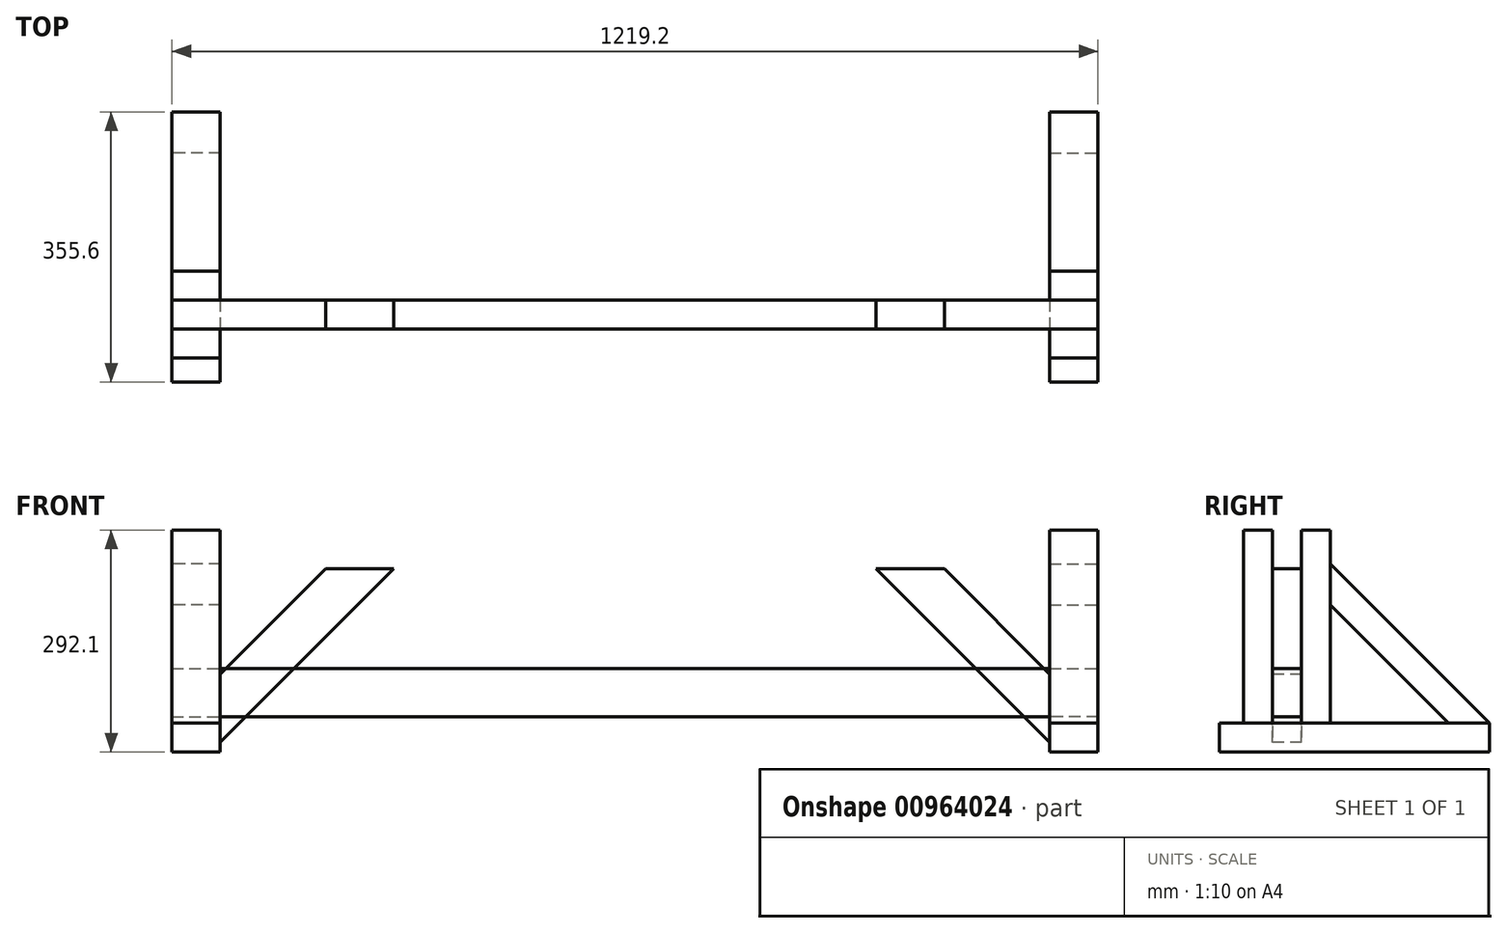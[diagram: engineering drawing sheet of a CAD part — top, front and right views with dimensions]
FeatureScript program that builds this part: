
annotation { "Feature Type Name" : "Feature", "Feature Type Description" : "" }
export const myFeature = defineFeature(function(context is Context, id is Id, definition is map)
    precondition{}
    {
        {
            assignVariable(context, id + "F0", {"name" : "shortLength", "anyValue" : 8});
        }
        {
            var Q0;
            Q0=qCreatedBy(makeId("Top.planeOp"),FACE);
            var sketch = newSketch(context, id + "F1", { "sketchPlane" : qUnion([Q0])});
            skLineSegment(sketch, "E0.bottom", {"start": v(-609.6, 254) * mm, "end": v(-546.1, 254) * mm});
            skLineSegment(sketch, "E0.top", {"start": v(-609.6, -101.6) * mm, "end": v(-546.1, -101.6) * mm});
            skLineSegment(sketch, "E0.left", {"start": v(-609.6, 254) * mm, "end": v(-609.6, -101.6) * mm});
            skLineSegment(sketch, "E0.right", {"start": v(-546.1, 254) * mm, "end": v(-546.1, -101.6) * mm});
            skLineSegment(sketch, "E1", {"start": v(-577.85, 254) * mm, "end": v(-577.85, -101.6) * mm, "construction": true});
            skSolve(sketch);
        }
        {
            var Q0;
            Q0=makeQuery(id+"F1.imprint","IMPRINT",FACE,{"disambiguationData":[TD([[makeQuery(id+"F1.imprint","IMPRINT",EDGE,{"derivedFrom":sQuery(id+"F1.wireOp",EDGE,"E0.bottom")}),-1.0]])]});
            extrude(context, id + "F2", {"entities" : qUnion([Q0]), "depth" : 38.1 * mm, "offsetDistance" : 25.4 * mm});
        }
        {
            var Q0;
            Q0=makeQuery(id+"F2.opExtrude","CAP_FACE",FACE,{"disambiguationData":[OSD([sQuery(id+"F1.wireOp",EDGE,"E0.bottom"),sQuery(id+"F1.wireOp",EDGE,"E0.top"),sQuery(id+"F1.wireOp",EDGE,"E0.left"),sQuery(id+"F1.wireOp",EDGE,"E0.right")])],"isStart":false});
            var sketch = newSketch(context, id + "F3", { "sketchPlane" : qUnion([Q0])});
            skLineSegment(sketch, "E2.bottom", {"start": v(-609.6, 6.35) * mm, "end": v(-546.1, 6.35) * mm});
            skLineSegment(sketch, "E2.top", {"start": v(-609.6, -31.75) * mm, "end": v(-546.1, -31.75) * mm});
            skLineSegment(sketch, "E2.left", {"start": v(-609.6, 6.35) * mm, "end": v(-609.6, -31.75) * mm});
            skLineSegment(sketch, "E2.right", {"start": v(-546.1, 6.35) * mm, "end": v(-546.1, -31.75) * mm});
            skSolve(sketch);
        }
        {
            var Q0;
            Q0=makeQuery(id+"F3.imprint","IMPRINT",FACE,{"disambiguationData":[TD([[makeQuery(id+"F3.imprint","IMPRINT",EDGE,{"derivedFrom":sQuery(id+"F3.wireOp",EDGE,"E2.bottom")}),-1.0]])]});
            extrude(context, id + "F4", {"entities" : qUnion([Q0]), "depth" : (getVariable(context, 'shortLength')) * mm, "offsetDistance" : 25.4 * mm});
        }
        {
            var Q0;
            Q0=makeQuery(id+"F4.opExtrude","SWEPT_BODY",BODY,{"disambiguationData":[OSD([sQuery(id+"F3.wireOp",EDGE,"E2.bottom"),sQuery(id+"F3.wireOp",EDGE,"E2.top"),sQuery(id+"F3.wireOp",EDGE,"E2.left"),sQuery(id+"F3.wireOp",EDGE,"E2.right")])]});
            var Q1;
            Q1=makeQuery(id+"F2.opExtrude","SWEPT_BODY",BODY,{"disambiguationData":[OSD([sQuery(id+"F1.wireOp",EDGE,"E0.bottom"),sQuery(id+"F1.wireOp",EDGE,"E0.top"),sQuery(id+"F1.wireOp",EDGE,"E0.left"),sQuery(id+"F1.wireOp",EDGE,"E0.right")])]});
            var Q2;
            Q2=qCreatedBy(makeId("Right.planeOp"),FACE);
            mirror(context, id + "F5", {"entities" : qUnion([Q0, Q1]), "mirrorPlane" : qUnion([Q2])});
        }
        {
            var Q0;
            Q0=makeQuery(id+"F4.opExtrude","CAP_FACE",FACE,{"disambiguationData":[OSD([sQuery(id+"F3.wireOp",EDGE,"E2.bottom"),sQuery(id+"F3.wireOp",EDGE,"E2.top"),sQuery(id+"F3.wireOp",EDGE,"E2.left"),sQuery(id+"F3.wireOp",EDGE,"E2.right")])],"isStart":false});
            var sketch = newSketch(context, id + "F6", { "sketchPlane" : qUnion([Q0])});
            skLineSegment(sketch, "E3.bottom", {"start": v(-609.6, 6.35) * mm, "end": v(609.6, 6.35) * mm});
            skLineSegment(sketch, "E3.top", {"start": v(-609.6, -31.75) * mm, "end": v(609.6, -31.75) * mm});
            skLineSegment(sketch, "E3.left", {"start": v(-609.6, 6.35) * mm, "end": v(-609.6, -31.75) * mm});
            skLineSegment(sketch, "E3.right", {"start": v(609.6, 6.35) * mm, "end": v(609.6, -31.75) * mm});
            skSolve(sketch);
        }
        {
            var Q0;
            Q0 = qSketchRegion(id + "F6", true);
            extrude(context, id + "F7", {"entities" : qUnion([Q0]), "depth" : 63.5 * mm, "offsetDistance" : 25.4 * mm});
        }
        {
            var Q0;
            Q0=makeQuery(id+"F4.opExtrude","SWEPT_FACE",FACE,{"disambiguationData":[OSD([sQuery(id+"F3.wireOp",EDGE,"E2.top")])]});
            var sketch = newSketch(context, id + "F8", { "sketchPlane" : qUnion([Q0])});
            skLineSegment(sketch, "E4", {"start": v(-609.6, 304.8) * mm, "end": v(-609.6, 0) * mm});
            skLineSegment(sketch, "E5", {"start": v(-546.1, 241.3) * mm, "end": v(-546.1, 38.1) * mm, "construction": true});
            skLineSegment(sketch, "E6", {"start": v(-546.1, 241.3) * mm, "end": v(-342.9, 241.3) * mm, "construction": true});
            skLineSegment(sketch, "E7", {"start": v(-546.1, 102.5) * mm, "end": v(-407.3, 241.3) * mm});
            skLineSegment(sketch, "E8", {"start": v(-407.3, 241.3) * mm, "end": v(-317.5, 241.3) * mm});
            skLineSegment(sketch, "E9", {"start": v(-317.5, 241.3) * mm, "end": v(-546.1, 12.7) * mm});
            skLineSegment(sketch, "E10", {"start": v(-546.1, 12.7) * mm, "end": v(-546.1, 102.5) * mm});
            skLineSegment(sketch, "E11", {"start": v(-407.3, 241.3) * mm, "end": v(-362.4, 196.4) * mm, "construction": true});
            skSolve(sketch);
        }
        {
            var Q0;
            Q0 = qSketchRegion(id + "F8", true);
            extrude(context, id + "F9", {"entities" : qUnion([Q0]), "oppositeDirection" : true, "depth" : 38.1 * mm, "offsetDistance" : 25.4 * mm});
        }
        {
            var Q0;
            Q0=makeQuery(id+"F9.opExtrude","SWEPT_BODY",BODY,{"disambiguationData":[OSD([sQuery(id+"F8.wireOp",EDGE,"E7"),sQuery(id+"F8.wireOp",EDGE,"E8"),sQuery(id+"F8.wireOp",EDGE,"E9"),sQuery(id+"F8.wireOp",EDGE,"E10")])]});
            var Q1;
            Q1=qCreatedBy(makeId("Right.planeOp"),FACE);
            mirror(context, id + "F10", {"entities" : qUnion([Q0]), "mirrorPlane" : qUnion([Q1])});
        }
        {
            var Q0;
            Q0=makeQuery(id+"F2.opExtrude","CAP_FACE",FACE,{"disambiguationData":[OSD([sQuery(id+"F1.wireOp",EDGE,"E0.bottom"),sQuery(id+"F1.wireOp",EDGE,"E0.top"),sQuery(id+"F1.wireOp",EDGE,"E0.left"),sQuery(id+"F1.wireOp",EDGE,"E0.right")])],"isStart":false});
            var sketch = newSketch(context, id + "F11", { "sketchPlane" : qUnion([Q0])});
            skLineSegment(sketch, "E12.bottom", {"start": v(-609.6, -31.75) * mm, "end": v(-546.1, -31.75) * mm});
            skLineSegment(sketch, "E12.top", {"start": v(-609.6, -69.85) * mm, "end": v(-546.1, -69.85) * mm});
            skLineSegment(sketch, "E12.left", {"start": v(-609.6, -31.75) * mm, "end": v(-609.6, -69.85) * mm});
            skLineSegment(sketch, "E12.right", {"start": v(-546.1, -31.75) * mm, "end": v(-546.1, -69.85) * mm});
            skLineSegment(sketch, "E13.bottom", {"start": v(-609.6, 44.45) * mm, "end": v(-546.1, 44.45) * mm});
            skLineSegment(sketch, "E13.top", {"start": v(-609.6, 6.35) * mm, "end": v(-546.1, 6.35) * mm});
            skLineSegment(sketch, "E13.left", {"start": v(-609.6, 44.45) * mm, "end": v(-609.6, 6.35) * mm});
            skLineSegment(sketch, "E13.right", {"start": v(-546.1, 44.45) * mm, "end": v(-546.1, 6.35) * mm});
            skSolve(sketch);
        }
        {
            var Q0;
            Q0 = qSketchRegion(id + "F11", true);
            extrude(context, id + "F12", {"entities" : qUnion([Q0]), "depth" : 254 * mm, "offsetDistance" : 25.4 * mm});
        }
        {
            var Q0;
            Q0=makeQuery(id+"F12.opExtrude","SWEPT_BODY",BODY,{"disambiguationData":[OSD([sQuery(id+"F11.wireOp",EDGE,"E13.bottom"),sQuery(id+"F11.wireOp",EDGE,"E13.top"),sQuery(id+"F11.wireOp",EDGE,"E13.left"),sQuery(id+"F11.wireOp",EDGE,"E13.right")])]});
            var Q1;
            Q1=makeQuery(id+"F12.opExtrude","SWEPT_BODY",BODY,{"disambiguationData":[OSD([sQuery(id+"F11.wireOp",EDGE,"E12.bottom"),sQuery(id+"F11.wireOp",EDGE,"E12.top"),sQuery(id+"F11.wireOp",EDGE,"E12.left"),sQuery(id+"F11.wireOp",EDGE,"E12.right")])]});
            var Q2;
            Q2=qCreatedBy(makeId("Right.planeOp"),FACE);
            mirror(context, id + "F13", {"entities" : qUnion([Q0, Q1]), "mirrorPlane" : qUnion([Q2])});
        }
        {
            var Q0;
            Q0=makeQuery(id+"F5.opPattern","COPY",FACE,{"derivedFrom":makeQuery(id+"F2.opExtrude","SWEPT_FACE",FACE,{"disambiguationData":[OSD([sQuery(id+"F1.wireOp",EDGE,"E0.left")])]}),"instanceName":"1"});
            var sketch = newSketch(context, id + "F14", { "sketchPlane" : qUnion([Q0])});
            skLineSegment(sketch, "E14", {"start": v(200.12, 38.1) * mm, "end": v(44.45, 193.77) * mm});
            skLineSegment(sketch, "E15", {"start": v(44.45, 193.77) * mm, "end": v(44.45, 247.65) * mm});
            skLineSegment(sketch, "E16", {"start": v(44.45, 247.65) * mm, "end": v(254, 38.1) * mm});
            skLineSegment(sketch, "E17", {"start": v(254, 38.1) * mm, "end": v(200.12, 38.1) * mm});
            skLineSegment(sketch, "E18", {"start": v(200.12, 38.1) * mm, "end": v(227.06, 65.04) * mm, "construction": true});
            skSolve(sketch);
        }
        {
            var Q0;
            Q0 = qSketchRegion(id + "F14", true);
            extrude(context, id + "F15", {"entities" : qUnion([Q0]), "oppositeDirection" : true, "depth" : 63.5 * mm, "offsetDistance" : 25.4 * mm});
        }
        {
            var Q0;
            Q0=makeQuery(id+"F15.opExtrude","SWEPT_BODY",BODY,{"disambiguationData":[OSD([sQuery(id+"F14.wireOp",EDGE,"E14"),sQuery(id+"F14.wireOp",EDGE,"E15"),sQuery(id+"F14.wireOp",EDGE,"E16"),sQuery(id+"F14.wireOp",EDGE,"E17")])]});
            var Q1;
            Q1=qCreatedBy(makeId("Right.planeOp"),FACE);
            mirror(context, id + "F16", {"entities" : qUnion([Q0]), "mirrorPlane" : qUnion([Q1])});
        }
    });
